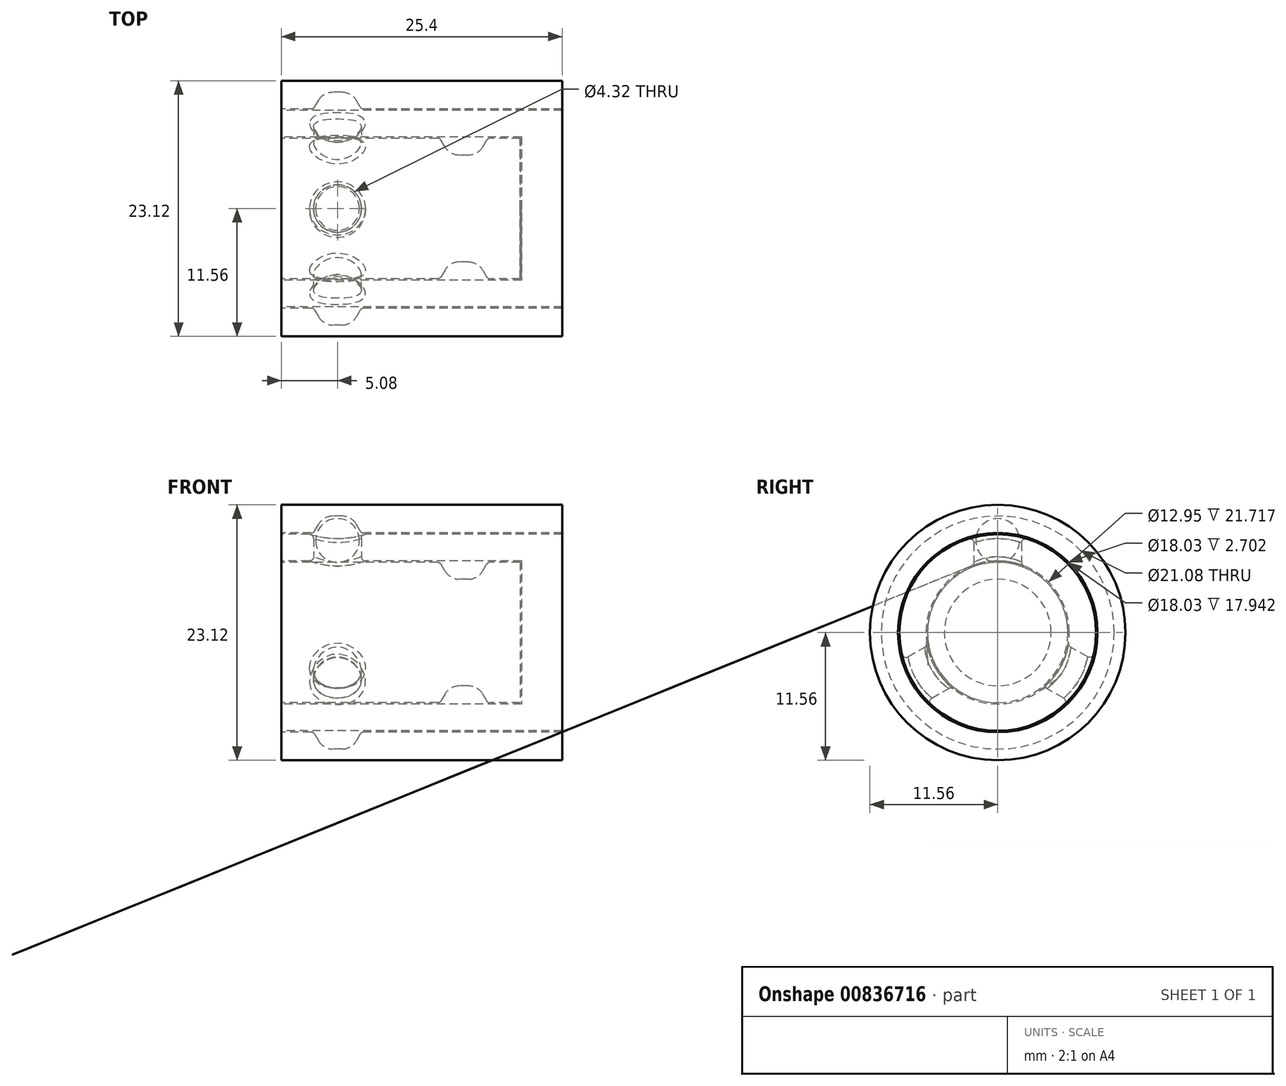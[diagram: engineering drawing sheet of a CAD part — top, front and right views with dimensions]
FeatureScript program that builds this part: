
annotation { "Feature Type Name" : "Feature", "Feature Type Description" : "" }
export const myFeature = defineFeature(function(context is Context, id is Id, definition is map)
    precondition{}
    {
        {
            var Q0;
            Q0=qCreatedBy(makeId("Front.planeOp"),FACE);
            var sketch = newSketch(context, id + "F0", { "sketchPlane" : qUnion([Q0])});
            skLineSegment(sketch, "E0", {"start": v(-25.4, 0) * mm, "end": v(-3.81, 0) * mm});
            skLineSegment(sketch, "E1", {"start": v(-3.68, 6.48) * mm, "end": v(-25.4, 6.48) * mm});
            skLineSegment(sketch, "E2", {"start": v(0, 8.9) * mm, "end": v(-25.4, 8.89) * mm});
            skLineSegment(sketch, "E3", {"start": v(-25.4, 6.48) * mm, "end": v(-25.4, 8.89) * mm});
            skLineSegment(sketch, "E4", {"start": v(-3.68, 0) * mm, "end": v(0, 0) * mm});
            skLineSegment(sketch, "E5", {"start": v(0, 0) * mm, "end": v(0, 8.9) * mm});
            skLineSegment(sketch, "E6.bottom", {"start": v(-25.4, 9.02) * mm, "end": v(-22.48, 9.02) * mm});
            skLineSegment(sketch, "E6.top", {"start": v(-25.4, 11.56) * mm, "end": v(0, 11.56) * mm});
            skLineSegment(sketch, "E6.left", {"start": v(-25.4, 9.02) * mm, "end": v(-25.4, 11.56) * mm});
            skLineSegment(sketch, "E6.right", {"start": v(0, 9.02) * mm, "end": v(0, 11.56) * mm});
            skLineSegment(sketch, "E7", {"start": v(-3.68, 0) * mm, "end": v(-3.68, 6.48) * mm});
            skLineSegment(sketch, "E8", {"start": v(-3.81, 0) * mm, "end": v(-3.81, 6.35) * mm});
            skLineSegment(sketch, "E9", {"start": v(-3.81, 6.35) * mm, "end": v(-6.73, 6.35) * mm});
            skLineSegment(sketch, "E10", {"start": v(-25.4, 6.35) * mm, "end": v(-25.4, 0) * mm});
            skArc(sketch, "E11", {"start": v(-22.3, 8.33) * mm, "mid": v(-20.32, 6.35) * mm, "end": v(-18.34, 8.33) * mm});
            skLineSegment(sketch, "E12", {"start": v(-22.3, 8.33) * mm, "end": v(-18.34, 8.33) * mm});
            skLineSegment(sketch, "E13", {"start": v(-7.62, 4.83) * mm, "end": v(-10.16, 4.83) * mm});
            skLineSegment(sketch, "E14.trimOffspring", {"start": v(-11.05, 6.35) * mm, "end": v(-25.4, 6.35) * mm});
            skLineSegment(sketch, "E15", {"start": v(-6.73, 6.35) * mm, "end": v(-7.62, 4.83) * mm});
            skLineSegment(sketch, "E16", {"start": v(-11.05, 6.35) * mm, "end": v(-10.16, 4.83) * mm});
            skLineSegment(sketch, "E17", {"start": v(-8.9, 4.83) * mm, "end": v(-8.9, 8.9) * mm, "construction": true});
            skCircle(sketch, "E18", {"center": v(-8.9, 7.04) * mm, "radius": 1.98 * mm, "construction": true});
            skArc(sketch, "E19", {"start": v(-18.34, 8.33) * mm, "mid": v(-20.32, 10.31) * mm, "end": v(-22.3, 8.33) * mm, "construction": true});
            skLineSegment(sketch, "E20", {"start": v(-20.32, 8.33) * mm, "end": v(-20.32, 10.54) * mm, "construction": true});
            skLineSegment(sketch, "E21", {"start": v(-21.59, 10.54) * mm, "end": v(-19.05, 10.54) * mm});
            skLineSegment(sketch, "E22", {"start": v(-19.05, 10.54) * mm, "end": v(-18.16, 9.02) * mm});
            skLineSegment(sketch, "E23", {"start": v(-21.59, 10.54) * mm, "end": v(-22.48, 9.02) * mm});
            skLineSegment(sketch, "E24.trimOffspring", {"start": v(-18.16, 9.02) * mm, "end": v(0, 9.02) * mm});
            skSolve(sketch);
        }
        {
            var Q0;
            Q0=makeQuery(id+"F0.imprint","IMPRINT",FACE,{"disambiguationData":[TD([[makeQuery(id+"F0.imprint","IMPRINT",EDGE,{"derivedFrom":sQuery(id+"F0.wireOp",EDGE,"E0")}),1.0]])]});
            var Q1;
            Q1=makeQuery(id+"F0.imprint","IMPRINT",FACE,{"disambiguationData":[TD([[makeQuery(id+"F0.imprint","IMPRINT",EDGE,{"derivedFrom":sQuery(id+"F0.wireOp",EDGE,"E6.bottom")}),1.0]])]});
            var Q2;
            Q2=makeQuery(id+"F0.imprint","IMPRINT",FACE,{"disambiguationData":[TD([[makeQuery(id+"F0.imprint","IMPRINT",EDGE,{"derivedFrom":sQuery(id+"F0.wireOp",EDGE,"E2")}),1.0]])]});
            var Q3;
            {var subQ4=sQuery(id+"F0.wireOp",EDGE,"E12");Q3=makeQuery(id+"F0.imprint","IMPRINT",FACE,{"disambiguationData":[TD([[makeQuery(id+"F0.imprint","IMPRINT",EDGE,{"derivedFrom":subQ4}),-1.0]])]});}
            var Q4;
            Q4=sQuery(id+"F0.wireOp",EDGE,"E0");
            revolve(context, id + "F1", {"surfaceOperationType" : NewSurfaceOperationType.NEW, "entities" : qUnion([Q0, Q1, Q2, Q3]), "axis" : qUnion([Q4]), "revolveType" : RevolveType.FULL});
        }
        {
            var Q0;
            {var subQ4=sQuery(id+"F0.wireOp",EDGE,"E12");Q0=makeQuery(id+"F0.imprint","IMPRINT",FACE,{"disambiguationData":[TD([[makeQuery(id+"F0.imprint","IMPRINT",EDGE,{"derivedFrom":subQ4}),-1.0]])]});}
            var Q1;
            {var subQ0=sQuery(id+"F0.wireOp",EDGE,"E11");var subQ1=sQuery(id+"F0.wireOp",EDGE,"E1");var subQ2=makeQuery(id+"F0.imprint","INTERSECT",VERTEX,{"disambiguationData":[OD(0.0)],"derivedFrom":[subQ1,subQ0]});Q1=makeQuery(id+"F0.imprint","IMPRINT",FACE,{"disambiguationData":[TD([[makeQuery(id+"F0.imprint","IMPRINT",EDGE,{"disambiguationData":[TD([[subQ2,-1.0]])],"derivedFrom":subQ1}),1.0]])]});}
            var Q2;
            Q2=sQuery(id+"F0.wireOp",EDGE,"E12");
            revolve(context, id + "F2", {"surfaceOperationType" : NewSurfaceOperationType.NEW, "entities" : qUnion([Q0, Q1]), "axis" : qUnion([Q2]), "revolveType" : RevolveType.FULL});
        }
        {
            var Q0;
            Q0=makeQuery(id+"F1.opRevolve","SWEPT_EDGE",EDGE,{"disambiguationData":[OSD([sQuery(id+"F0.wireOp",EDGE,"E13"),sQuery(id+"F0.wireOp",EDGE,"E16")])]});
            var Q1;
            Q1=makeQuery(id+"F1.opRevolve","SWEPT_EDGE",EDGE,{"disambiguationData":[OSD([sQuery(id+"F0.wireOp",EDGE,"E13"),sQuery(id+"F0.wireOp",EDGE,"E15")])]});
            var Q2;
            Q2=makeQuery(id+"F1.opRevolve","SWEPT_EDGE",EDGE,{"disambiguationData":[OSD([sQuery(id+"F0.wireOp",EDGE,"E21"),sQuery(id+"F0.wireOp",EDGE,"E22")])]});
            var Q3;
            Q3=makeQuery(id+"F1.opRevolve","SWEPT_EDGE",EDGE,{"disambiguationData":[OSD([sQuery(id+"F0.wireOp",EDGE,"E21"),sQuery(id+"F0.wireOp",EDGE,"E23")])]});
            fillet(context, id + "F3", {"entities" : qUnion([Q0, Q1, Q2, Q3]), "radius" : 1.52 * mm, "tangentPropagation" : true, "allowEdgeOverflow" : false});
        }
        {
            var Q0;
            Q0=makeQuery(id+"F1.opRevolve","SWEPT_EDGE",EDGE,{"disambiguationData":[OSD([sQuery(id+"F0.wireOp",EDGE,"E14.trimOffspring"),sQuery(id+"F0.wireOp",EDGE,"E16")])]});
            var Q1;
            Q1=makeQuery(id+"F1.opRevolve","SWEPT_EDGE",EDGE,{"disambiguationData":[OSD([sQuery(id+"F0.wireOp",EDGE,"E9"),sQuery(id+"F0.wireOp",EDGE,"E15")])]});
            var Q2;
            Q2=makeQuery(id+"F1.opRevolve","SWEPT_EDGE",EDGE,{"disambiguationData":[OSD([sQuery(id+"F0.wireOp",EDGE,"E22"),sQuery(id+"F0.wireOp",EDGE,"E24.trimOffspring")])]});
            var Q3;
            Q3=makeQuery(id+"F1.opRevolve","SWEPT_EDGE",EDGE,{"disambiguationData":[OSD([sQuery(id+"F0.wireOp",EDGE,"E6.bottom"),sQuery(id+"F0.wireOp",EDGE,"E23")])]});
            fillet(context, id + "F4", {"entities" : qUnion([Q0, Q1, Q2, Q3]), "radius" : 0.38 * mm, "tangentPropagation" : true, "allowEdgeOverflow" : false});
        }
        {
            var Q0;
            Q0=qCreatedBy(makeId("Top.planeOp"),FACE);
            var sketch = newSketch(context, id + "F5", { "sketchPlane" : qUnion([Q0])});
            skCircle(sketch, "E25", {"center": v(-20.32, 0) * mm, "radius": 2.16 * mm});
            skSolve(sketch);
        }
        {
            var Q0;
            Q0 = qSketchRegion(id + "F5", true);
            extrude(context, id + "F6", {"entities" : qUnion([Q0]), "endBound" : BoundingType.THROUGH_ALL, "depth" : 25.4 * mm, "offsetDistance" : 25.4 * mm});
        }
        {
            var Q0;
            Q0=makeQuery(id+"F6.opExtrude","SWEPT_BODY",BODY,{"disambiguationData":[OSD([sQuery(id+"F5.wireOp",EDGE,"E25")])]});
            var Q1;
            Q1=makeQuery(id+"F1.opRevolve","SWEPT_FACE",FACE,{"disambiguationData":[OSD([sQuery(id+"F0.wireOp",EDGE,"E6.top")])]});
            circularPattern(context, id + "F7", {"entities" : qUnion([Q0]), "axis" : qUnion([Q1]), "angle" : 360 * degree, "instanceCount" : 3, "equalSpace" : true});
        }
        {
            var Q0;
            Q0=makeQuery(id+"F6.opExtrude","SWEPT_BODY",BODY,{"disambiguationData":[OSD([sQuery(id+"F5.wireOp",EDGE,"E25")])]});
            var Q1;
            Q1=makeQuery(id+"F7.opPattern","COPY",BODY,{"derivedFrom":makeQuery(id+"F6.opExtrude","SWEPT_BODY",BODY,{"disambiguationData":[OSD([sQuery(id+"F5.wireOp",EDGE,"E25")])]}),"instanceName":"2"});
            var Q2;
            Q2=makeQuery(id+"F7.opPattern","COPY",BODY,{"derivedFrom":makeQuery(id+"F6.opExtrude","SWEPT_BODY",BODY,{"disambiguationData":[OSD([sQuery(id+"F5.wireOp",EDGE,"E25")])]}),"instanceName":"1"});
            var Q3;
            Q3=makeQuery(id+"F1.opRevolve","SWEPT_BODY",BODY,{"disambiguationData":[OSD([sQuery(id+"F0.wireOp",EDGE,"E1"),sQuery(id+"F0.wireOp",EDGE,"E2"),sQuery(id+"F0.wireOp",EDGE,"E3"),sQuery(id+"F0.wireOp",EDGE,"E4"),sQuery(id+"F0.wireOp",EDGE,"E5"),sQuery(id+"F0.wireOp",EDGE,"E7")])]});
            booleanBodies(context, id + "F8", {"operationType" : BooleanOperationType.SUBTRACTION, "tools" : qUnion([Q0, Q1, Q2]), "targets" : qUnion([Q3])});
        }
        {
            var Q0;
            Q0=makeQuery(id+"F8.opBoolean","INTERSECT",EDGE,{"derivedFrom":[makeQuery(id+"F1.opRevolve","SWEPT_FACE",FACE,{"disambiguationData":[OSD([sQuery(id+"F0.wireOp",EDGE,"E2")])]}),makeQuery(id+"F6.opExtrude","SWEPT_FACE",FACE,{"disambiguationData":[OSD([sQuery(id+"F5.wireOp",EDGE,"E25")])]})]});
            var Q1;
            Q1=makeQuery(id+"F8.opBoolean","INTERSECT",EDGE,{"derivedFrom":[makeQuery(id+"F1.opRevolve","SWEPT_FACE",FACE,{"disambiguationData":[OSD([sQuery(id+"F0.wireOp",EDGE,"E2")])]}),makeQuery(id+"F7.opPattern","COPY",FACE,{"derivedFrom":makeQuery(id+"F6.opExtrude","SWEPT_FACE",FACE,{"disambiguationData":[OSD([sQuery(id+"F5.wireOp",EDGE,"E25")])]}),"instanceName":"2"})]});
            var Q2;
            Q2=makeQuery(id+"F8.opBoolean","INTERSECT",EDGE,{"derivedFrom":[makeQuery(id+"F1.opRevolve","SWEPT_FACE",FACE,{"disambiguationData":[OSD([sQuery(id+"F0.wireOp",EDGE,"E1")])]}),makeQuery(id+"F7.opPattern","COPY",FACE,{"derivedFrom":makeQuery(id+"F6.opExtrude","SWEPT_FACE",FACE,{"disambiguationData":[OSD([sQuery(id+"F5.wireOp",EDGE,"E25")])]}),"instanceName":"2"})]});
            var Q3;
            Q3=makeQuery(id+"F8.opBoolean","INTERSECT",EDGE,{"derivedFrom":[makeQuery(id+"F1.opRevolve","SWEPT_FACE",FACE,{"disambiguationData":[OSD([sQuery(id+"F0.wireOp",EDGE,"E1")])]}),makeQuery(id+"F7.opPattern","COPY",FACE,{"derivedFrom":makeQuery(id+"F6.opExtrude","SWEPT_FACE",FACE,{"disambiguationData":[OSD([sQuery(id+"F5.wireOp",EDGE,"E25")])]}),"instanceName":"1"})]});
            var Q4;
            Q4=makeQuery(id+"F8.opBoolean","INTERSECT",EDGE,{"derivedFrom":[makeQuery(id+"F1.opRevolve","SWEPT_FACE",FACE,{"disambiguationData":[OSD([sQuery(id+"F0.wireOp",EDGE,"E2")])]}),makeQuery(id+"F7.opPattern","COPY",FACE,{"derivedFrom":makeQuery(id+"F6.opExtrude","SWEPT_FACE",FACE,{"disambiguationData":[OSD([sQuery(id+"F5.wireOp",EDGE,"E25")])]}),"instanceName":"1"})]});
            var Q5;
            Q5=makeQuery(id+"F8.opBoolean","INTERSECT",EDGE,{"derivedFrom":[makeQuery(id+"F1.opRevolve","SWEPT_FACE",FACE,{"disambiguationData":[OSD([sQuery(id+"F0.wireOp",EDGE,"E1")])]}),makeQuery(id+"F6.opExtrude","SWEPT_FACE",FACE,{"disambiguationData":[OSD([sQuery(id+"F5.wireOp",EDGE,"E25")])]})]});
            fillet(context, id + "F9", {"entities" : qUnion([Q0, Q1, Q2, Q3, Q4, Q5]), "radius" : 0.38 * mm, "tangentPropagation" : true, "allowEdgeOverflow" : false});
        }
    });
